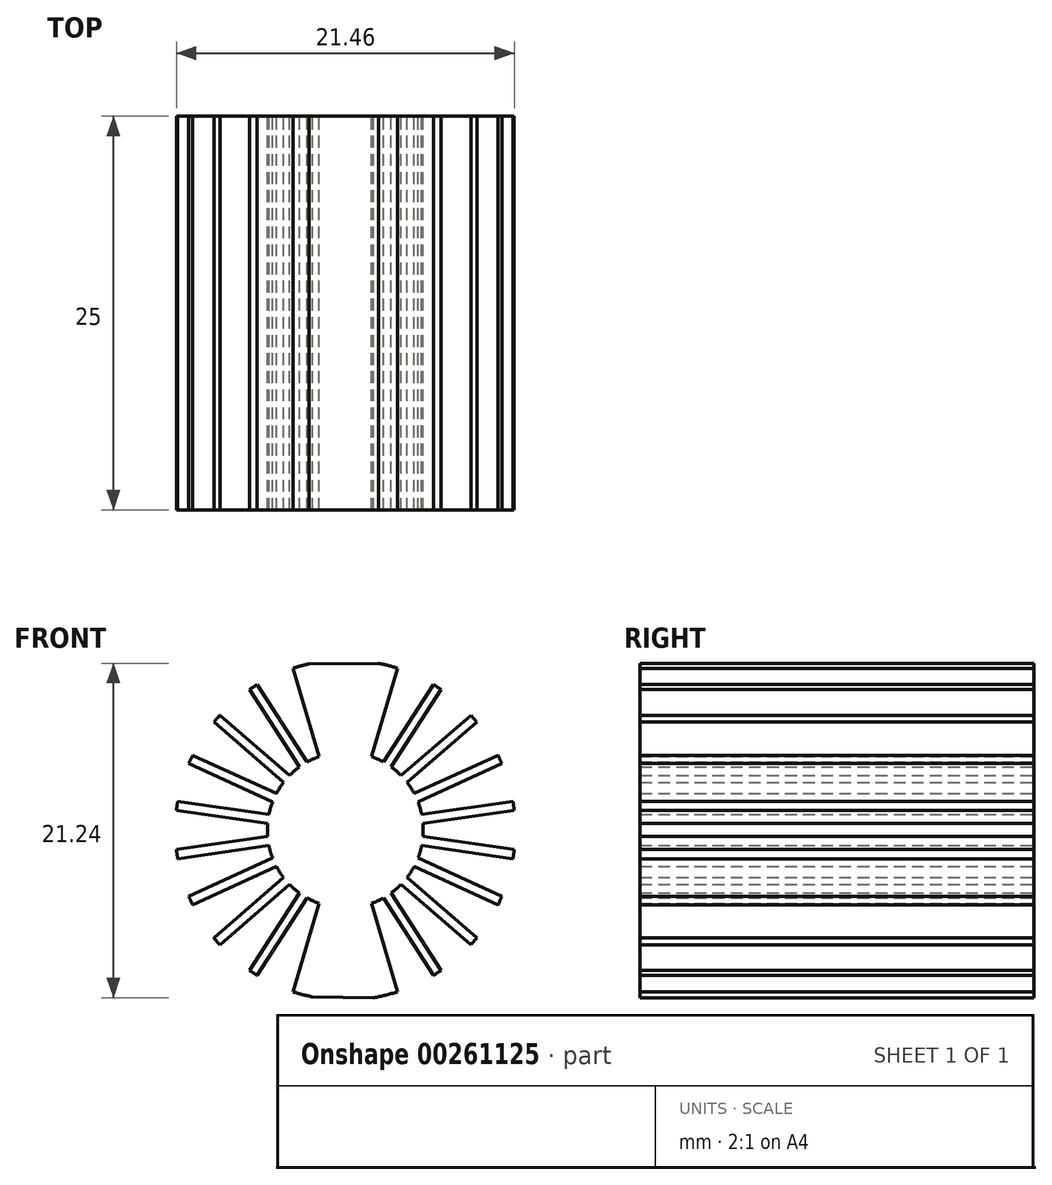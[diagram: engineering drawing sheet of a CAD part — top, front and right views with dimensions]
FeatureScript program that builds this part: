
annotation { "Feature Type Name" : "Feature", "Feature Type Description" : "" }
export const myFeature = defineFeature(function(context is Context, id is Id, definition is map)
    precondition{}
    {
        {
            var Q0;
            Q0=qCreatedBy(makeId("Front.planeOp"),FACE);
            var sketch = newSketch(context, id + "F0", { "sketchPlane" : qUnion([Q0])});
            skArc(sketch, "E0", {"start": v(-5.6, 9.24) * mm, "mid": v(-5.84, 9.09) * mm, "end": v(-6.08, 8.92) * mm});
            skArc(sketch, "E1", {"start": v(-1.67, 4.66) * mm, "mid": v(-2.06, 4.5) * mm, "end": v(-2.43, 4.31) * mm});
            skLineSegment(sketch, "E2.1.0", {"start": v(-3.32, 10.28) * mm, "end": v(-1.67, 4.66) * mm});
            skLineSegment(sketch, "E2.2.0", {"start": v(-6.08, 8.92) * mm, "end": v(-2.92, 4) * mm});
            skLineSegment(sketch, "E2.2.1", {"start": v(-5.6, 9.24) * mm, "end": v(-2.43, 4.31) * mm});
            skLineSegment(sketch, "E2.3.0", {"start": v(-8.35, 6.85) * mm, "end": v(-3.93, 3.02) * mm});
            skLineSegment(sketch, "E2.3.1", {"start": v(-7.97, 7.3) * mm, "end": v(-3.54, 3.46) * mm});
            skLineSegment(sketch, "E2.4.0", {"start": v(-9.94, 4.22) * mm, "end": v(-4.62, 1.79) * mm});
            skLineSegment(sketch, "E2.4.1", {"start": v(-9.7, 4.75) * mm, "end": v(-4.37, 2.32) * mm});
            skLineSegment(sketch, "E2.5.0", {"start": v(-10.73, 1.25) * mm, "end": v(-4.93, 0.41) * mm});
            skLineSegment(sketch, "E2.5.1", {"start": v(-10.64, 1.83) * mm, "end": v(-4.85, 1) * mm});
            skLineSegment(sketch, "E2.6.0", {"start": v(-10.64, -1.83) * mm, "end": v(-4.85, -1) * mm});
            skLineSegment(sketch, "E2.6.1", {"start": v(-10.73, -1.25) * mm, "end": v(-4.93, -0.41) * mm});
            skLineSegment(sketch, "E2.7.0", {"start": v(-9.7, -4.75) * mm, "end": v(-4.37, -2.32) * mm});
            skLineSegment(sketch, "E2.7.1", {"start": v(-9.94, -4.22) * mm, "end": v(-4.62, -1.79) * mm});
            skLineSegment(sketch, "E2.8.0", {"start": v(-7.97, -7.3) * mm, "end": v(-3.54, -3.46) * mm});
            skLineSegment(sketch, "E2.8.1", {"start": v(-8.35, -6.85) * mm, "end": v(-3.93, -3.02) * mm});
            skLineSegment(sketch, "E2.9.0", {"start": v(-5.6, -9.24) * mm, "end": v(-2.43, -4.31) * mm});
            skLineSegment(sketch, "E2.9.1", {"start": v(-6.08, -8.92) * mm, "end": v(-2.92, -4) * mm});
            skLineSegment(sketch, "E2.10.1", {"start": v(-3.32, -10.28) * mm, "end": v(-1.67, -4.66) * mm});
            skLineSegment(sketch, "E2.12.0", {"start": v(3.32, -10.28) * mm, "end": v(1.67, -4.66) * mm});
            skLineSegment(sketch, "E2.13.0", {"start": v(6.08, -8.92) * mm, "end": v(2.92, -4) * mm});
            skLineSegment(sketch, "E2.13.1", {"start": v(5.6, -9.24) * mm, "end": v(2.43, -4.31) * mm});
            skLineSegment(sketch, "E2.14.0", {"start": v(8.35, -6.85) * mm, "end": v(3.93, -3.02) * mm});
            skLineSegment(sketch, "E2.14.1", {"start": v(7.97, -7.3) * mm, "end": v(3.54, -3.46) * mm});
            skLineSegment(sketch, "E2.15.0", {"start": v(9.94, -4.22) * mm, "end": v(4.62, -1.79) * mm});
            skLineSegment(sketch, "E2.15.1", {"start": v(9.7, -4.75) * mm, "end": v(4.37, -2.32) * mm});
            skLineSegment(sketch, "E2.16.0", {"start": v(10.73, -1.25) * mm, "end": v(4.93, -0.41) * mm});
            skLineSegment(sketch, "E2.16.1", {"start": v(10.64, -1.83) * mm, "end": v(4.85, -1) * mm});
            skLineSegment(sketch, "E2.17.0", {"start": v(10.64, 1.83) * mm, "end": v(4.85, 1) * mm});
            skLineSegment(sketch, "E2.17.1", {"start": v(10.73, 1.25) * mm, "end": v(4.93, 0.41) * mm});
            skLineSegment(sketch, "E2.18.0", {"start": v(9.7, 4.75) * mm, "end": v(4.37, 2.32) * mm});
            skLineSegment(sketch, "E2.18.1", {"start": v(9.94, 4.22) * mm, "end": v(4.62, 1.79) * mm});
            skLineSegment(sketch, "E2.19.0", {"start": v(7.97, 7.3) * mm, "end": v(3.54, 3.46) * mm});
            skLineSegment(sketch, "E2.19.1", {"start": v(8.35, 6.85) * mm, "end": v(3.93, 3.02) * mm});
            skLineSegment(sketch, "E2.20.0", {"start": v(5.6, 9.24) * mm, "end": v(2.43, 4.31) * mm});
            skLineSegment(sketch, "E2.20.1", {"start": v(6.08, 8.92) * mm, "end": v(2.92, 4) * mm});
            skLineSegment(sketch, "E2.21.1", {"start": v(3.32, 10.28) * mm, "end": v(1.67, 4.66) * mm});
            skArc(sketch, "E3.trimOffspring", {"start": v(3.32, 10.28) * mm, "mid": v(2.72, 10.45) * mm, "end": v(2.1, 10.6) * mm});
            skArc(sketch, "E4.trimOffspring", {"start": v(-3.32, -10.28) * mm, "mid": v(-2.7, -10.46) * mm, "end": v(-2.07, -10.6) * mm});
            skArc(sketch, "E5.trimOffspring", {"start": v(5.6, -9.24) * mm, "mid": v(5.84, -9.09) * mm, "end": v(6.08, -8.92) * mm});
            skArc(sketch, "E6.trimOffspring", {"start": v(7.97, -7.3) * mm, "mid": v(8.16, -7.07) * mm, "end": v(8.35, -6.85) * mm});
            skArc(sketch, "E7.trimOffspring", {"start": v(9.7, -4.75) * mm, "mid": v(9.82, -4.49) * mm, "end": v(9.94, -4.22) * mm});
            skArc(sketch, "E8.trimOffspring", {"start": v(10.64, -1.83) * mm, "mid": v(10.7, -1.54) * mm, "end": v(10.73, -1.25) * mm});
            skArc(sketch, "E9.trimOffspring", {"start": v(10.73, 1.25) * mm, "mid": v(10.7, 1.54) * mm, "end": v(10.64, 1.83) * mm});
            skArc(sketch, "E10.trimOffspring", {"start": v(9.94, 4.22) * mm, "mid": v(9.82, 4.49) * mm, "end": v(9.7, 4.75) * mm});
            skArc(sketch, "E11.trimOffspring", {"start": v(8.35, 6.85) * mm, "mid": v(8.16, 7.07) * mm, "end": v(7.97, 7.3) * mm});
            skArc(sketch, "E12.trimOffspring", {"start": v(6.08, 8.92) * mm, "mid": v(5.84, 9.09) * mm, "end": v(5.6, 9.24) * mm});
            skArc(sketch, "E13.trimOffspring", {"start": v(-7.97, 7.3) * mm, "mid": v(-8.16, 7.07) * mm, "end": v(-8.35, 6.85) * mm});
            skArc(sketch, "E14.trimOffspring", {"start": v(-9.7, 4.75) * mm, "mid": v(-9.82, 4.49) * mm, "end": v(-9.94, 4.22) * mm});
            skArc(sketch, "E15.trimOffspring", {"start": v(-10.64, 1.83) * mm, "mid": v(-10.7, 1.54) * mm, "end": v(-10.73, 1.25) * mm});
            skArc(sketch, "E16.trimOffspring", {"start": v(-10.73, -1.25) * mm, "mid": v(-10.7, -1.54) * mm, "end": v(-10.64, -1.83) * mm});
            skArc(sketch, "E17.trimOffspring", {"start": v(-9.94, -4.22) * mm, "mid": v(-9.82, -4.49) * mm, "end": v(-9.7, -4.75) * mm});
            skArc(sketch, "E18.trimOffspring", {"start": v(-8.35, -6.85) * mm, "mid": v(-8.16, -7.07) * mm, "end": v(-7.97, -7.3) * mm});
            skArc(sketch, "E19.trimOffspring", {"start": v(-6.08, -8.92) * mm, "mid": v(-5.84, -9.09) * mm, "end": v(-5.6, -9.24) * mm});
            skArc(sketch, "E20.trimOffspring", {"start": v(-2.92, 4) * mm, "mid": v(-3.24, 3.74) * mm, "end": v(-3.54, 3.46) * mm});
            skArc(sketch, "E21.trimOffspring", {"start": v(-3.93, 3.02) * mm, "mid": v(-4.16, 2.68) * mm, "end": v(-4.37, 2.32) * mm});
            skArc(sketch, "E22.trimOffspring", {"start": v(-4.62, 1.79) * mm, "mid": v(-4.75, 1.4) * mm, "end": v(-4.85, 1) * mm});
            skArc(sketch, "E23.trimOffspring", {"start": v(-4.93, 0.41) * mm, "mid": v(-4.95, 0) * mm, "end": v(-4.93, -0.41) * mm});
            skArc(sketch, "E24.trimOffspring", {"start": v(-4.85, -1) * mm, "mid": v(-4.75, -1.4) * mm, "end": v(-4.62, -1.79) * mm});
            skArc(sketch, "E25.trimOffspring", {"start": v(-4.37, -2.32) * mm, "mid": v(-4.16, -2.68) * mm, "end": v(-3.93, -3.02) * mm});
            skArc(sketch, "E26.trimOffspring", {"start": v(-3.54, -3.46) * mm, "mid": v(-3.24, -3.74) * mm, "end": v(-2.92, -4) * mm});
            skArc(sketch, "E27.trimOffspring", {"start": v(-2.43, -4.31) * mm, "mid": v(-2.06, -4.5) * mm, "end": v(-1.67, -4.66) * mm});
            skArc(sketch, "E28.trimOffspring", {"start": v(1.67, -4.66) * mm, "mid": v(2.06, -4.5) * mm, "end": v(2.43, -4.31) * mm});
            skArc(sketch, "E29.trimOffspring", {"start": v(2.92, -4) * mm, "mid": v(3.24, -3.74) * mm, "end": v(3.54, -3.46) * mm});
            skArc(sketch, "E30.trimOffspring", {"start": v(3.93, -3.02) * mm, "mid": v(4.16, -2.68) * mm, "end": v(4.37, -2.32) * mm});
            skArc(sketch, "E31.trimOffspring", {"start": v(4.62, -1.79) * mm, "mid": v(4.75, -1.4) * mm, "end": v(4.85, -1) * mm});
            skArc(sketch, "E32.trimOffspring", {"start": v(4.93, -0.41) * mm, "mid": v(4.95, 0) * mm, "end": v(4.93, 0.41) * mm});
            skArc(sketch, "E33.trimOffspring", {"start": v(4.85, 1) * mm, "mid": v(4.75, 1.4) * mm, "end": v(4.62, 1.79) * mm});
            skArc(sketch, "E34.trimOffspring", {"start": v(4.37, 2.32) * mm, "mid": v(4.16, 2.68) * mm, "end": v(3.93, 3.02) * mm});
            skArc(sketch, "E35.trimOffspring", {"start": v(3.54, 3.46) * mm, "mid": v(3.24, 3.74) * mm, "end": v(2.92, 4) * mm});
            skArc(sketch, "E36.trimOffspring", {"start": v(2.43, 4.31) * mm, "mid": v(2.06, 4.5) * mm, "end": v(1.67, 4.66) * mm});
            skLineSegment(sketch, "E37", {"start": v(0, 0) * mm, "end": v(0, 10.55) * mm});
            skLineSegment(sketch, "E38", {"start": v(0, 0) * mm, "end": v(0, -10.55) * mm});
            skPoint(sketch, "E38.endSnap0", {"position": v(0, -10.8) * mm});
            skLineSegment(sketch, "E39", {"start": v(-2.07, -10.6) * mm, "end": v(1.78, -10.65) * mm});
            skArc(sketch, "E40.trimOffspring", {"start": v(1.78, -10.65) * mm, "mid": v(2.56, -10.5) * mm, "end": v(3.32, -10.28) * mm});
            skLineSegment(sketch, "E41", {"start": v(-2.31, 10.55) * mm, "end": v(2.1, 10.6) * mm});
            skArc(sketch, "E42.trimOffspring", {"start": v(-2.31, 10.55) * mm, "mid": v(-2.82, 10.43) * mm, "end": v(-3.32, 10.28) * mm});
            skSolve(sketch);
        }
        {
            var Q0;
            Q0 = qSketchRegion(id + "F0", true);
            extrude(context, id + "F1", {"entities" : qUnion([Q0]), "depth" : 25 * mm});
        }
    });
